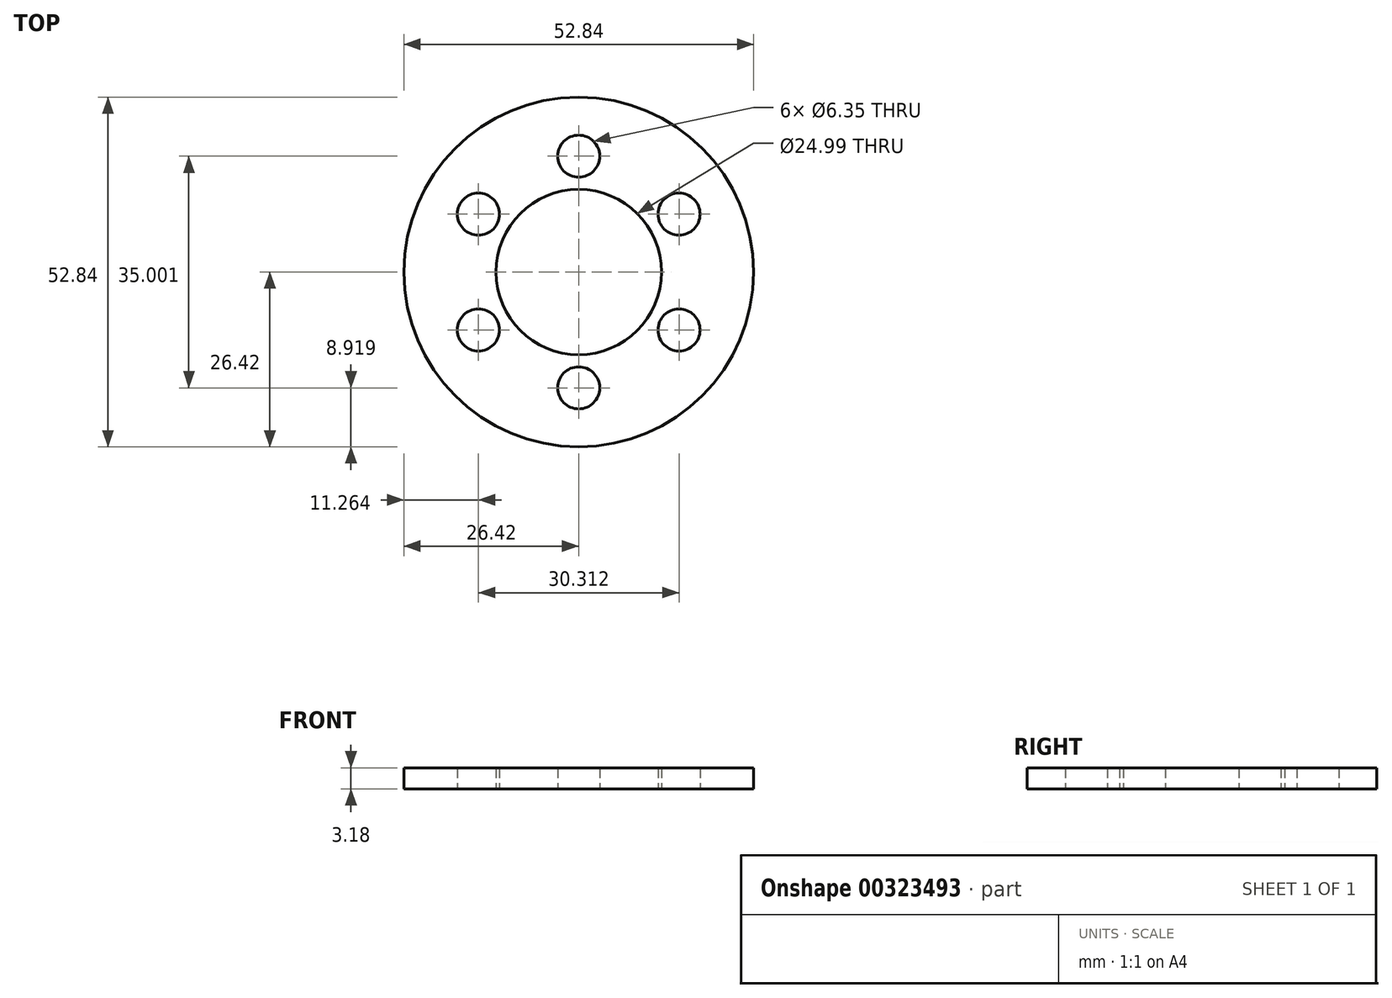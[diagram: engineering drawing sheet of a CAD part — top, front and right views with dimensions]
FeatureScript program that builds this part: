
annotation { "Feature Type Name" : "Feature", "Feature Type Description" : "" }
export const myFeature = defineFeature(function(context is Context, id is Id, definition is map)
    precondition{}
    {
        {
            var Q0;
            Q0=qCreatedBy(makeId("Top.planeOp"),FACE);
            var sketch = newSketch(context, id + "F0", { "sketchPlane" : qUnion([Q0])});
            skCircle(sketch, "E0", {"center": v(0, 0) * mm, "radius": 26.42 * mm});
            skCircle(sketch, "E1", {"center": v(0, 0) * mm, "radius": 12.5 * mm});
            skLineSegment(sketch, "E2", {"start": v(0, 0) * mm, "end": v(0, 17.5) * mm});
            skLineSegment(sketch, "E3", {"start": v(0, 0) * mm, "end": v(0, -17.5) * mm});
            skCircle(sketch, "E4", {"center": v(0, 17.5) * mm, "radius": 3.18 * mm});
            skCircle(sketch, "E5", {"center": v(0, -17.5) * mm, "radius": 3.18 * mm});
            skLineSegment(sketch, "E6", {"start": v(0, 0) * mm, "end": v(-15.16, 8.75) * mm});
            skLineSegment(sketch, "E7", {"start": v(-15.16, 8.75) * mm, "end": v(0, 0) * mm});
            skLineSegment(sketch, "E8", {"start": v(0, 0) * mm, "end": v(15.16, -8.75) * mm});
            skLineSegment(sketch, "E9", {"start": v(15.16, -8.75) * mm, "end": v(0, 0) * mm});
            skLineSegment(sketch, "E10", {"start": v(0, 0) * mm, "end": v(15.16, 8.75) * mm});
            skLineSegment(sketch, "E11", {"start": v(15.16, 8.75) * mm, "end": v(0, 0) * mm});
            skLineSegment(sketch, "E12", {"start": v(0, 0) * mm, "end": v(-15.16, -8.75) * mm});
            skCircle(sketch, "E13", {"center": v(-15.16, 8.75) * mm, "radius": 3.18 * mm});
            skCircle(sketch, "E14", {"center": v(15.16, 8.75) * mm, "radius": 3.18 * mm});
            skCircle(sketch, "E15", {"center": v(15.16, -8.75) * mm, "radius": 3.18 * mm});
            skCircle(sketch, "E16", {"center": v(-15.16, -8.75) * mm, "radius": 3.18 * mm});
            skSolve(sketch);
        }
        {
            var Q0;
            Q0=makeQuery(id+"F0.imprint","IMPRINT",FACE,{"disambiguationData":[TD([[makeQuery(id+"F0.imprint","IMPRINT",EDGE,{"derivedFrom":sQuery(id+"F0.wireOp",EDGE,"E0")}),1.0]])]});
            extrude(context, id + "F1", {"entities" : qUnion([Q0]), "depth" : 3.17 * mm});
        }
    });
